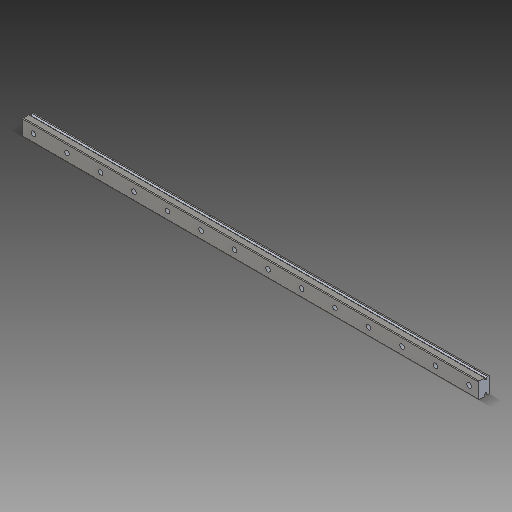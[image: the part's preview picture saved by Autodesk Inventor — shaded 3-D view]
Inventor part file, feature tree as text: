
AUTODESK INVENTOR PART (.ipt)
format: ipt  version: 2017.3 (Build 213256000, 256)  size: 187,904 bytes
history: native  units: mm
features: other x3, sketch x2
ambient origin geometry x8: Origin, YZ Plane, XZ Plane, XY Plane, X Axis, Y Axis, Z Axis, Center Point
bodies: Solid1 (feature_tree)
feature tree (5):
  other  "MGN12 Rail 300mm.ipt"
  other  "Solid1::MGN12 Rail 300mm.ipt"
  other  "TaggingFeature1"
  sketch  "Sketch1"  dims[d0=10.0mm]
  sketch  "Sketch3"
